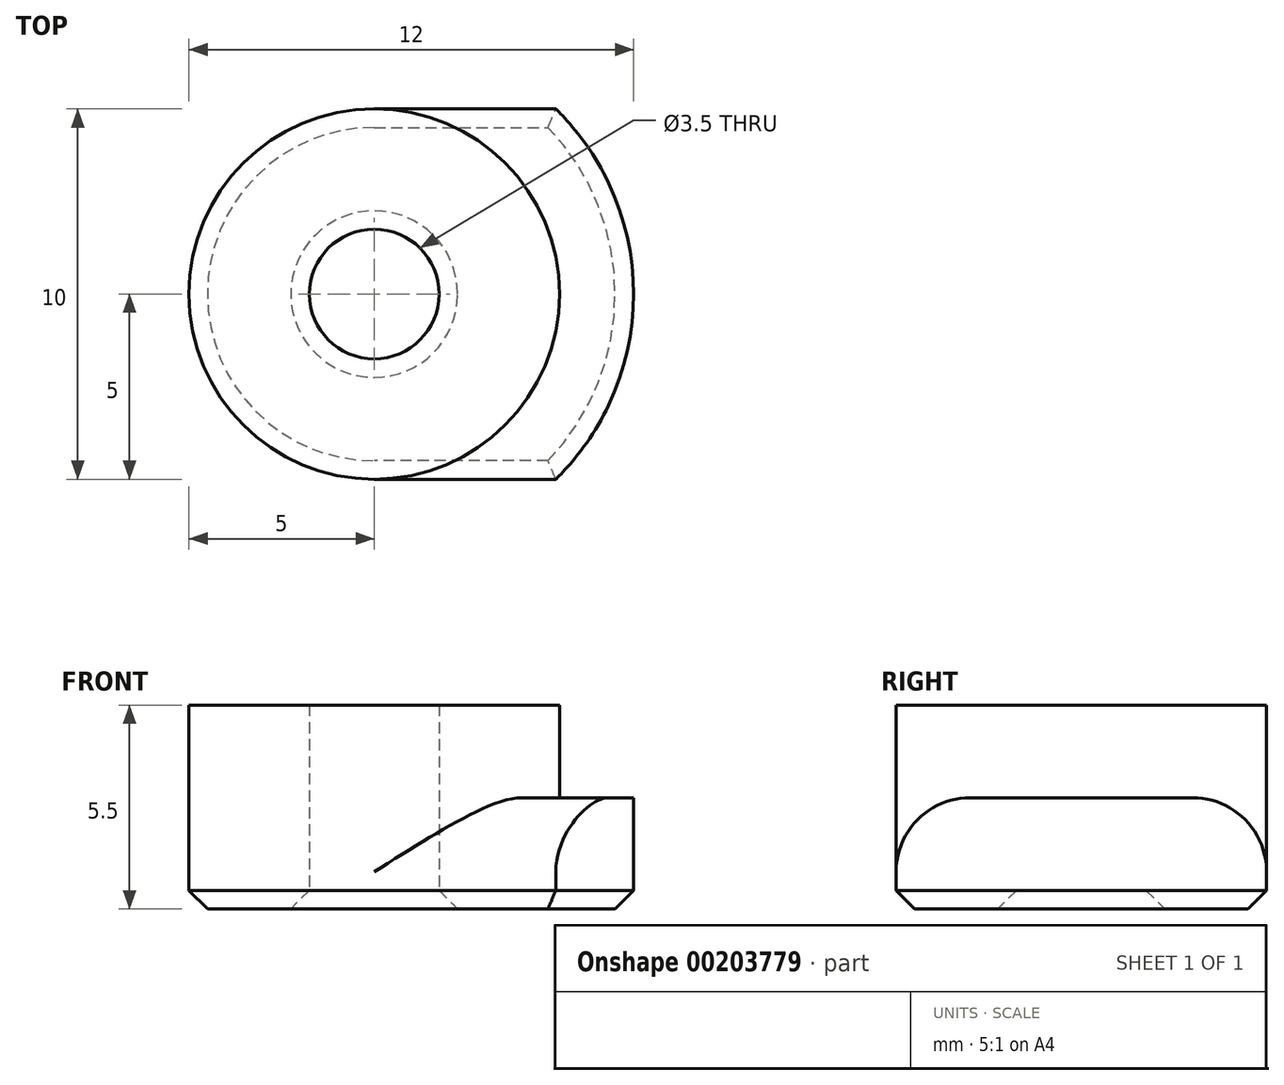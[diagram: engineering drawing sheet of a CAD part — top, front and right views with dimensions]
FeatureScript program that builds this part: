
annotation { "Feature Type Name" : "Feature", "Feature Type Description" : "" }
export const myFeature = defineFeature(function(context is Context, id is Id, definition is map)
    precondition{}
    {
        {
            var Q0;
            Q0=qCreatedBy(makeId("Top.planeOp"),FACE);
            var sketch = newSketch(context, id + "F0", { "sketchPlane" : qUnion([Q0])});
            skCircle(sketch, "E0", {"center": v(0, 0) * mm, "radius": 5 * mm});
            skCircle(sketch, "E1", {"center": v(0, 0) * mm, "radius": 1.75 * mm});
            skSolve(sketch);
        }
        {
            var Q0;
            Q0=makeQuery(id+"F0.imprint","IMPRINT",FACE,{"disambiguationData":[TD([[makeQuery(id+"F0.imprint","IMPRINT",EDGE,{"derivedFrom":sQuery(id+"F0.wireOp",EDGE,"E0")}),1.0]])]});
            extrude(context, id + "F1", {"entities" : qUnion([Q0]), "depth" : 5.5 * mm});
        }
        {
            var Q0;
            Q0=qCreatedBy(makeId("Top.planeOp"),FACE);
            var sketch = newSketch(context, id + "F2", { "sketchPlane" : qUnion([Q0])});
            skArc(sketch, "E2", {"start": v(4.9, -5) * mm, "mid": v(7, 0) * mm, "end": v(4.9, 5) * mm});
            skArc(sketch, "E3", {"start": v(0, -5) * mm, "mid": v(5, 0) * mm, "end": v(0, 5) * mm});
            skLineSegment(sketch, "E4", {"start": v(0, 5) * mm, "end": v(4.9, 5) * mm});
            skLineSegment(sketch, "E5", {"start": v(0, -5) * mm, "end": v(4.9, -5) * mm});
            skSolve(sketch);
        }
        {
            var Q0;
            Q0=makeQuery(id+"F2.imprint","IMPRINT",FACE,{"disambiguationData":[TD([[makeQuery(id+"F2.imprint","IMPRINT",EDGE,{"derivedFrom":sQuery(id+"F2.wireOp",EDGE,"E2")}),1.0]])]});
            extrude(context, id + "F3", {"entities" : qUnion([Q0]), "operationType" : NewBodyOperationType.ADD, "depth" : 3 * mm});
        }
        {
            var Q0;
            Q0=makeQuery(id+"F3.opExtrude","CAP_EDGE",EDGE,{"disambiguationData":[OSD([sQuery(id+"F2.wireOp",EDGE,"E5")])],"isStart":false});
            var Q1;
            Q1=makeQuery(id+"F3.opExtrude","CAP_EDGE",EDGE,{"disambiguationData":[OSD([sQuery(id+"F2.wireOp",EDGE,"E4")])],"isStart":false});
            fillet(context, id + "F4", {"entities" : qUnion([Q0, Q1]), "radius" : 2 * mm, "tangentPropagation" : true, "allowEdgeOverflow" : false});
        }
        {
            var Q0;
            Q0=makeQuery(id+"F3.boolean.opBoolean","MERGE",FACE,{"derivedFrom":[makeQuery(id+"F1.opExtrude","CAP_FACE",FACE,{"disambiguationData":[OSD([sQuery(id+"F0.wireOp",EDGE,"E0"),sQuery(id+"F0.wireOp",EDGE,"E1")])],"isStart":true}),makeQuery(id+"F3.opExtrude","CAP_FACE",FACE,{"disambiguationData":[OSD([sQuery(id+"F2.wireOp",EDGE,"E2"),sQuery(id+"F2.wireOp",EDGE,"E3"),sQuery(id+"F2.wireOp",EDGE,"E4"),sQuery(id+"F2.wireOp",EDGE,"E5")])],"isStart":true})]});
            chamfer(context, id + "F5", {"entities" : qUnion([Q0]), "width" : .5 * mm, "tangentPropagation" : true});
        }
    });
